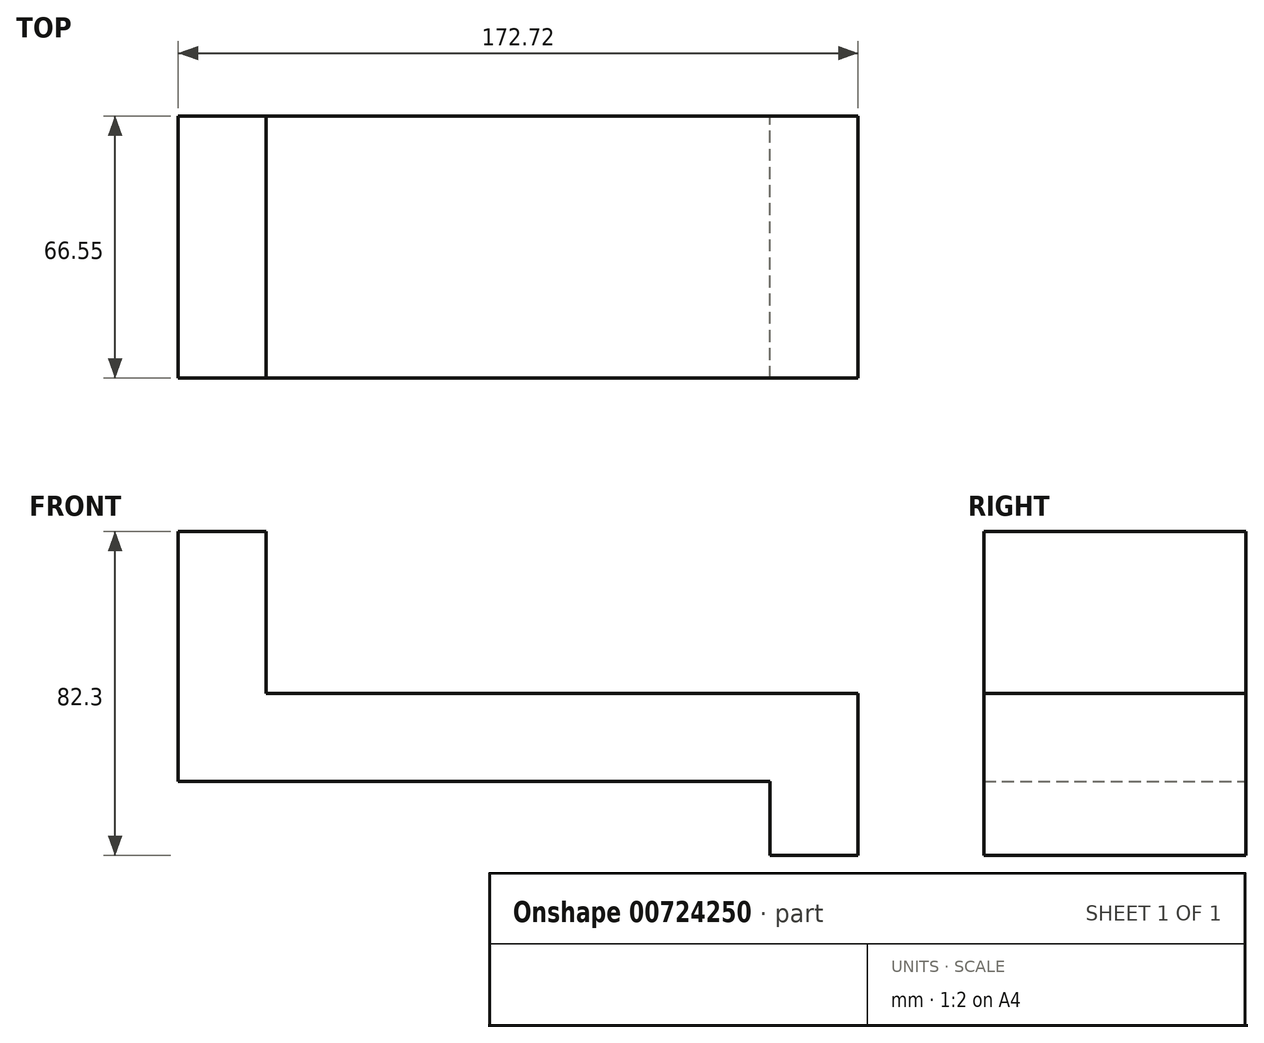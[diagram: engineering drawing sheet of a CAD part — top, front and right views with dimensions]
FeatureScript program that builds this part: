
annotation { "Feature Type Name" : "Feature", "Feature Type Description" : "" }
export const myFeature = defineFeature(function(context is Context, id is Id, definition is map)
    precondition{}
    {
        {
            var Q0;
            Q0=qCreatedBy(makeId("Front.planeOp"),FACE);
            var sketch = newSketch(context, id + "F0", { "sketchPlane" : qUnion([Q0])});
            skLineSegment(sketch, "E0", {"start": v(-67.33, 63.5) * mm, "end": v(-67.33, 0) * mm});
            skLineSegment(sketch, "E1", {"start": v(-67.33, 0) * mm, "end": v(83.03, 0) * mm});
            skLineSegment(sketch, "E2", {"start": v(83.03, 0) * mm, "end": v(83.03, -18.8) * mm});
            skLineSegment(sketch, "E3", {"start": v(83.03, -18.8) * mm, "end": v(105.39, -18.8) * mm});
            skLineSegment(sketch, "E4", {"start": v(105.39, -18.8) * mm, "end": v(105.39, 22.35) * mm});
            skLineSegment(sketch, "E5", {"start": v(105.39, 22.35) * mm, "end": v(-44.98, 22.35) * mm});
            skLineSegment(sketch, "E6", {"start": v(-44.98, 22.35) * mm, "end": v(-44.98, 63.5) * mm});
            skLineSegment(sketch, "E7", {"start": v(-44.98, 63.5) * mm, "end": v(-67.33, 63.5) * mm});
            skSolve(sketch);
        }
        {
            var Q0;
            Q0=makeQuery(id+"F0.imprint","IMPRINT",FACE,{"disambiguationData":[TD([[makeQuery(id+"F0.imprint","IMPRINT",EDGE,{"derivedFrom":sQuery(id+"F0.wireOp",EDGE,"E0")}),1.0]])]});
            extrude(context, id + "F1", {"entities" : qUnion([Q0]), "depth" : 66.55 * mm, "offsetDistance" : 25.4 * mm});
        }
    });
